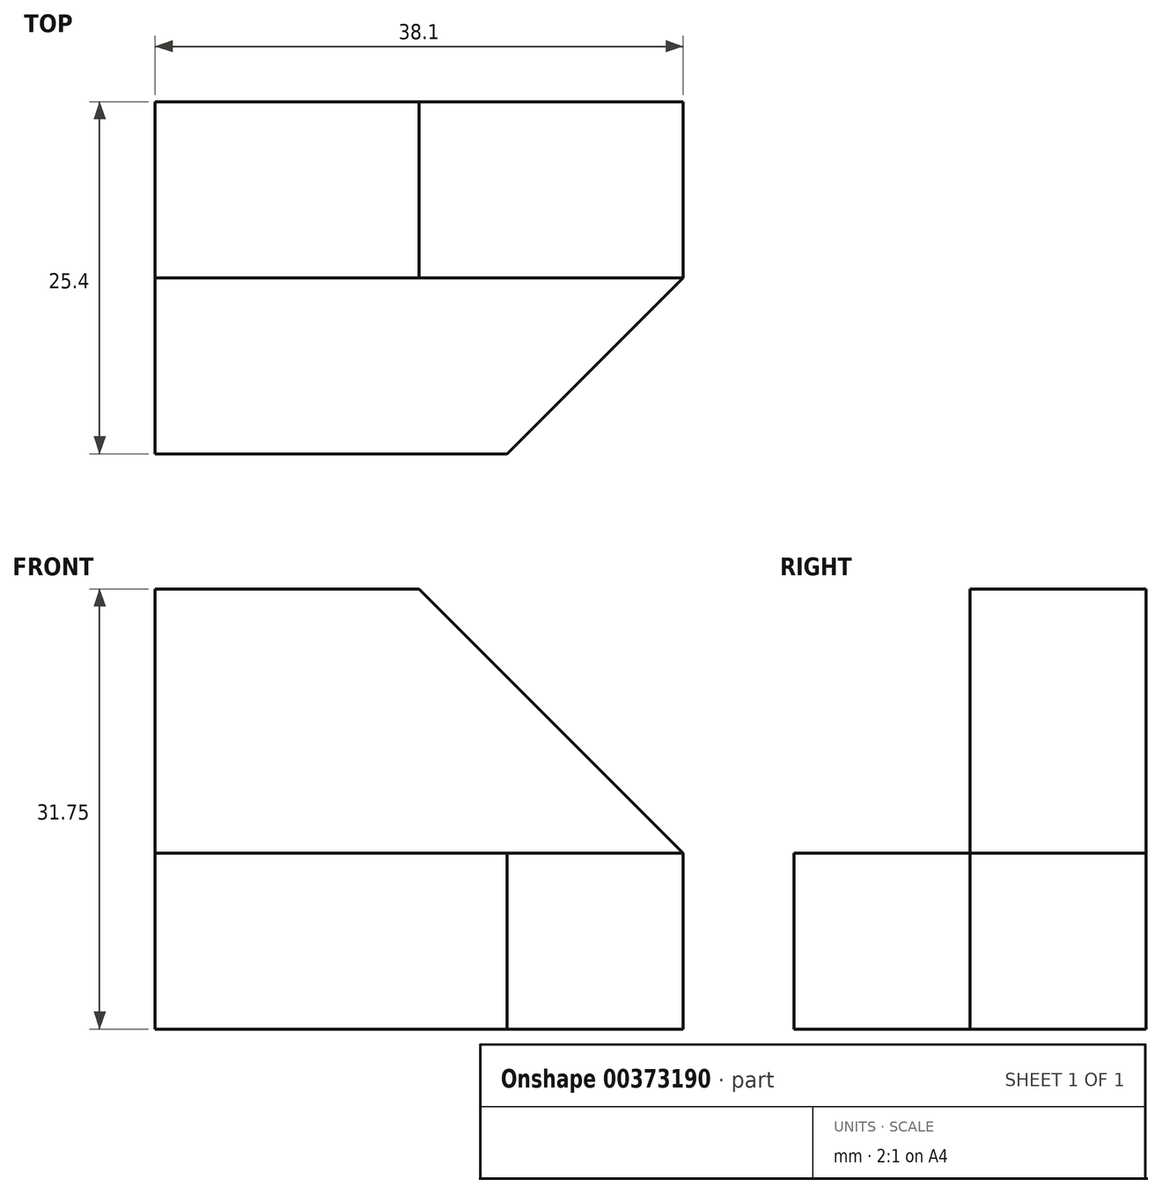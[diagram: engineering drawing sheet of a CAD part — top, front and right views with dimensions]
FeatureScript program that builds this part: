
annotation { "Feature Type Name" : "Feature", "Feature Type Description" : "" }
export const myFeature = defineFeature(function(context is Context, id is Id, definition is map)
    precondition{}
    {
        {
            var Q0;
            Q0=qCreatedBy(makeId("Right.planeOp"),FACE);
            var sketch = newSketch(context, id + "F0", { "sketchPlane" : qUnion([Q0])});
            skLineSegment(sketch, "E0", {"start": v(0, 0) * mm, "end": v(0, 31.75) * mm});
            skLineSegment(sketch, "E1", {"start": v(0, 31.75) * mm, "end": v(-12.7, 31.75) * mm});
            skLineSegment(sketch, "E2", {"start": v(-12.7, 31.75) * mm, "end": v(-12.7, 12.7) * mm});
            skLineSegment(sketch, "E3", {"start": v(-12.7, 12.7) * mm, "end": v(-25.4, 12.7) * mm});
            skLineSegment(sketch, "E4", {"start": v(-25.4, 12.7) * mm, "end": v(-25.4, 0) * mm});
            skLineSegment(sketch, "E5", {"start": v(-25.4, 0) * mm, "end": v(0, 0) * mm});
            skSolve(sketch);
        }
        {
            var Q0;
            Q0 = qSketchRegion(id + "F0", true);
            extrude(context, id + "F1", {"entities" : qUnion([Q0]), "depth" : 38.1 * mm});
        }
        {
            var Q0;
            Q0=makeQuery(id+"F1.opExtrude","CAP_EDGE",EDGE,{"disambiguationData":[OSD([sQuery(id+"F0.wireOp",EDGE,"E4")])],"isStart":false});
            chamfer(context, id + "F2", {"entities" : qUnion([Q0]), "width" : 12.7 * mm, "tangentPropagation" : true});
        }
        {
            var Q0;
            Q0=makeQuery(id+"F1.opExtrude","SWEPT_FACE",FACE,{"disambiguationData":[OSD([sQuery(id+"F0.wireOp",EDGE,"E1")])]});
            var sketch = newSketch(context, id + "F3", { "sketchPlane" : qUnion([Q0])});
            skLineSegment(sketch, "E6", {"start": v(19.05, -12.7) * mm, "end": v(55.73, -31.9) * mm});
            skLineSegment(sketch, "E7", {"start": v(55.73, -31.9) * mm, "end": v(38.1, -12.7) * mm});
            skLineSegment(sketch, "E8", {"start": v(38.1, -12.7) * mm, "end": v(19.05, -12.7) * mm});
            skSolve(sketch);
        }
        {
            var Q0;
            Q0=makeQuery(id+"F3.imprint","IMPRINT",FACE,{"disambiguationData":[TD([[makeQuery(id+"F3.imprint","IMPRINT",EDGE,{"derivedFrom":sQuery(id+"F3.wireOp",EDGE,"E6")}),1.0]])]});
            extrude(context, id + "F4", {"entities" : qUnion([Q0]), "operationType" : NewBodyOperationType.REMOVE, "depth" : 25.4 * mm});
        }
        {
            var Q0;
            Q0=makeQuery(id+"F1.opExtrude","CAP_EDGE",EDGE,{"disambiguationData":[OSD([sQuery(id+"F0.wireOp",EDGE,"E1")])],"isStart":false});
            chamfer(context, id + "F5", {"entities" : qUnion([Q0]), "width" : 19.05 * mm, "tangentPropagation" : true});
        }
    });
